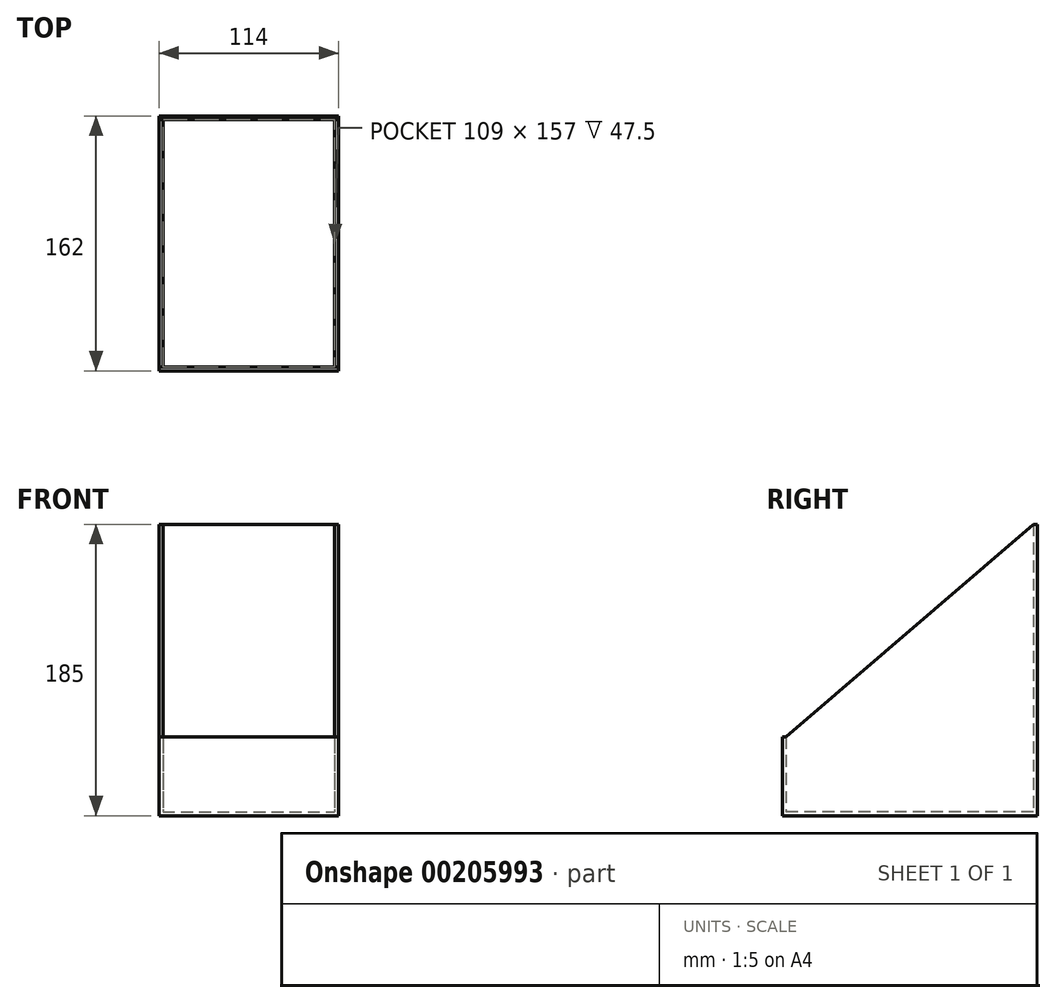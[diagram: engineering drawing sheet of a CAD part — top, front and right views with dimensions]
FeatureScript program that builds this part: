
annotation { "Feature Type Name" : "Feature", "Feature Type Description" : "" }
export const myFeature = defineFeature(function(context is Context, id is Id, definition is map)
    precondition{}
    {
        {
            var Q0;
            Q0=qCreatedBy(makeId("Top.planeOp"),FACE);
            var sketch = newSketch(context, id + "F0", { "sketchPlane" : qUnion([Q0])});
            skLineSegment(sketch, "E0.bottom", {"start": v(0, 0) * mm, "end": v(-114, 0) * mm});
            skLineSegment(sketch, "E0.top", {"start": v(0, -162) * mm, "end": v(-114, -162) * mm});
            skLineSegment(sketch, "E0.left", {"start": v(0, 0) * mm, "end": v(0, -162) * mm});
            skLineSegment(sketch, "E0.right", {"start": v(-114, 0) * mm, "end": v(-114, -162) * mm});
            skSolve(sketch);
        }
        {
            var Q0;
            Q0 = qSketchRegion(id + "F0", true);
            extrude(context, id + "F1", {"entities" : qUnion([Q0]), "depth" : 185 * mm});
        }
        {
            var Q0;
            Q0=qCreatedBy(makeId("Right.planeOp"),FACE);
            var sketch = newSketch(context, id + "F2", { "sketchPlane" : qUnion([Q0])});
            skLineSegment(sketch, "E1.0", {"start": v(0, 0) * mm, "end": v(-162, 0) * mm, "construction": true});
            skLineSegment(sketch, "E1.1", {"start": v(-162, 185) * mm, "end": v(-162, 0) * mm, "construction": true});
            skLineSegment(sketch, "E1.2", {"start": v(0, 185) * mm, "end": v(0, 0) * mm, "construction": true});
            skLineSegment(sketch, "E2.0", {"start": v(0, 50) * mm, "end": v(-162, 50) * mm, "construction": true});
            skLineSegment(sketch, "E3", {"start": v(-162, 50) * mm, "end": v(-159.5, 50) * mm});
            skLineSegment(sketch, "E4", {"start": v(0, 185) * mm, "end": v(-2.5, 185) * mm, "construction": true});
            skLineSegment(sketch, "E5", {"start": v(-159.5, 50) * mm, "end": v(-2.5, 185) * mm});
            skLineSegment(sketch, "E6", {"start": v(-2.5, 185) * mm, "end": v(-162, 185) * mm});
            skLineSegment(sketch, "E7", {"start": v(-162, 185) * mm, "end": v(-162, 50) * mm});
            skSolve(sketch);
        }
        {
            var Q0;
            Q0 = qSketchRegion(id + "F2", true);
            var Q1;
            Q1=makeQuery(id+"F1.opExtrude","SWEPT_FACE",FACE,{"disambiguationData":[OSD([sQuery(id+"F0.wireOp",EDGE,"E0.right")])]});
            extrude(context, id + "F3", {"entities" : qUnion([Q0]), "operationType" : NewBodyOperationType.REMOVE, "endBound" : BoundingType.UP_TO_SURFACE, "oppositeDirection" : true, "endBoundEntityFace" : qUnion([Q1]), "depth" : 25 * mm});
        }
        {
            var Q0;
            Q0=qCreatedBy(makeId("Top.planeOp"),FACE);
            cPlane(context, id + "F4", {"entities" : qUnion([Q0]), "cplaneType" : CPlaneType.OFFSET, "offset" : 2.5 * mm, "width" : 150 * mm, "height" : 150 * mm});
        }
        {
            var Q0;
            Q0=qCreatedBy(id+"F4.planeOp",FACE);
            var sketch = newSketch(context, id + "F5", { "sketchPlane" : qUnion([Q0])});
            skLineSegment(sketch, "E8.0.0", {"start": v(0, 0) * mm, "end": v(0, -162) * mm, "construction": true});
            skLineSegment(sketch, "E8.0.1", {"start": v(0, -162) * mm, "end": v(-114, -162) * mm, "construction": true});
            skLineSegment(sketch, "E8.0.2", {"start": v(-114, -162) * mm, "end": v(-114, 0) * mm, "construction": true});
            skLineSegment(sketch, "E8.0.3", {"start": v(-114, 0) * mm, "end": v(0, 0) * mm, "construction": true});
            skLineSegment(sketch, "E9.0", {"start": v(-2.5, -2.5) * mm, "end": v(-2.5, -159.5) * mm});
            skLineSegment(sketch, "E9.1", {"start": v(-111.5, -2.5) * mm, "end": v(-2.5, -2.5) * mm});
            skLineSegment(sketch, "E9.2", {"start": v(-111.5, -159.5) * mm, "end": v(-111.5, -2.5) * mm});
            skLineSegment(sketch, "E9.3", {"start": v(-2.5, -159.5) * mm, "end": v(-111.5, -159.5) * mm});
            skSolve(sketch);
        }
        {
            var Q0;
            Q0 = qSketchRegion(id + "F5", true);
            extrude(context, id + "F6", {"entities" : qUnion([Q0]), "operationType" : NewBodyOperationType.REMOVE, "endBound" : BoundingType.THROUGH_ALL, "depth" : 25 * mm});
        }
    });
